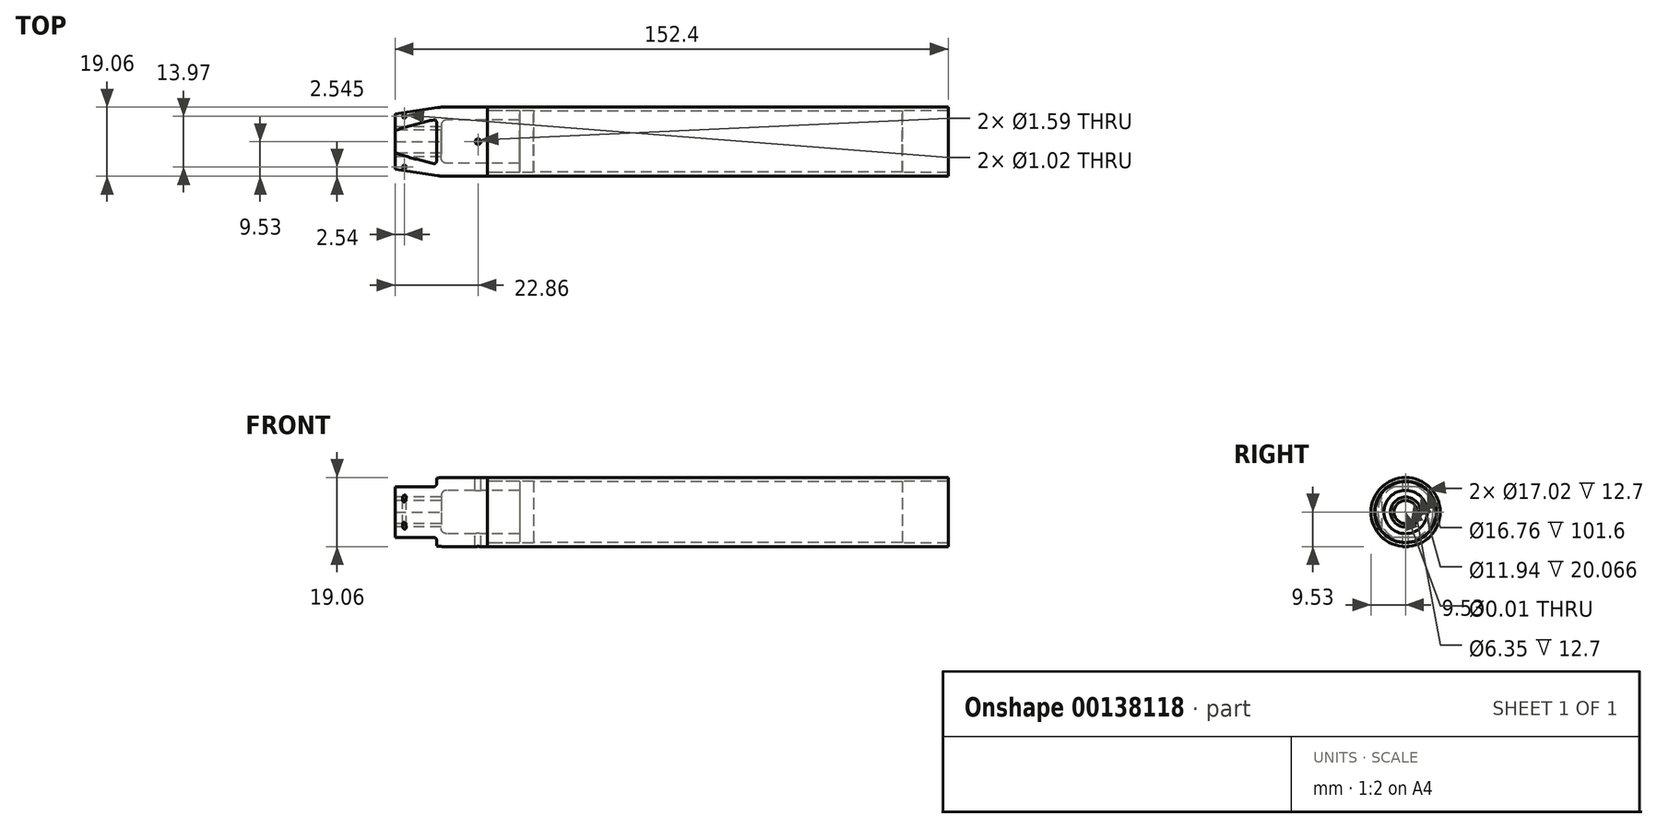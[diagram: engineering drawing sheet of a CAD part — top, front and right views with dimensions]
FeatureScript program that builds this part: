
annotation { "Feature Type Name" : "Feature", "Feature Type Description" : "" }
export const myFeature = defineFeature(function(context is Context, id is Id, definition is map)
    precondition{}
    {
        {
            var Q0;
            Q0=qCreatedBy(makeId("Top.planeOp"),FACE);
            var sketch = newSketch(context, id + "F0", { "sketchPlane" : qUnion([Q0])});
            skLineSegment(sketch, "E0.bottom", {"start": v(0, 9.53) * mm, "end": v(127, 9.53) * mm});
            skLineSegment(sketch, "E0.top", {"start": v(12.7, 8.38) * mm, "end": v(114.3, 8.38) * mm});
            skLineSegment(sketch, "E0.left", {"start": v(0, 9.53) * mm, "end": v(0, 8.5) * mm});
            skLineSegment(sketch, "E0.right", {"start": v(127, 9.53) * mm, "end": v(127, 8.5) * mm});
            skLineSegment(sketch, "E1", {"start": v(0, 8.5) * mm, "end": v(12.7, 8.5) * mm});
            skLineSegment(sketch, "E2", {"start": v(12.7, 8.5) * mm, "end": v(12.7, 8.38) * mm});
            skLineSegment(sketch, "E3", {"start": v(127, 8.5) * mm, "end": v(114.3, 8.5) * mm});
            skLineSegment(sketch, "E4", {"start": v(114.3, 8.5) * mm, "end": v(114.3, 8.38) * mm});
            skSolve(sketch);
        }
        {
            var Q0;
            Q0=qCreatedBy(makeId("Top.planeOp"),FACE);
            var sketch = newSketch(context, id + "F1", { "sketchPlane" : qUnion([Q0])});
            skLineSegment(sketch, "E5", {"start": v(0, 0) * mm, "end": v(25.4, 0) * mm});
            skSolve(sketch);
        }
        {
            var Q0;
            Q0 = qSketchRegion(id + "F0", true);
            var Q1;
            Q1=sQuery(id+"F1.wireOp",EDGE,"E5");
            revolve(context, id + "F2", {"entities" : qUnion([Q0]), "axis" : qUnion([Q1]), "revolveType" : RevolveType.FULL});
        }
        {
            var Q0;
            Q0=qCreatedBy(makeId("Top.planeOp"),FACE);
            var sketch = newSketch(context, id + "F3", { "sketchPlane" : qUnion([Q0])});
            skLineSegment(sketch, "E6", {"start": v(-25.4, 0) * mm, "end": v(-25.4, 7.62) * mm});
            skLineSegment(sketch, "E7", {"start": v(0, 9.53) * mm, "end": v(-12.7, 9.52) * mm});
            skLineSegment(sketch, "E8", {"start": v(-12.7, 9.52) * mm, "end": v(-25.4, 7.62) * mm});
            skLineSegment(sketch, "E9", {"start": v(-25.4, 0) * mm, "end": v(-12.7, 0) * mm});
            skLineSegment(sketch, "E10", {"start": v(-12.7, 0) * mm, "end": v(-12.7, 4.44) * mm});
            skLineSegment(sketch, "E11", {"start": v(-11.18, 5.97) * mm, "end": v(8.9, 5.97) * mm});
            skLineSegment(sketch, "E12", {"start": v(0, 8.5) * mm, "end": v(8.9, 8.5) * mm});
            skLineSegment(sketch, "E13.trimOffspring", {"start": v(0, 8.5) * mm, "end": v(0, 9.53) * mm});
            skPoint(sketch, "E14.0.start.orphan", {"position": v(0, -9.53) * mm});
            skLineSegment(sketch, "E15", {"start": v(8.9, 5.97) * mm, "end": v(8.9, 8.5) * mm});
            skPoint(sketch, "E16.visualSharp", {"position": v(-12.7, 5.97) * mm});
            skArc(sketch, "E16.filletArc", {"start": v(-11.18, 5.97) * mm, "mid": v(-12.25, 5.52) * mm, "end": v(-12.7, 4.44) * mm});
            skSolve(sketch);
        }
        {
            var Q0;
            Q0 = qSketchRegion(id + "F3", true);
            var Q1;
            Q1=sQuery(id+"F1.wireOp",EDGE,"E5");
            revolve(context, id + "F4", {"entities" : qUnion([Q0]), "axis" : qUnion([Q1]), "revolveType" : RevolveType.FULL});
        }
        {
            var Q0;
            Q0=makeQuery(id+"F4.opRevolve","SWEPT_FACE",FACE,{"disambiguationData":[OSD([sQuery(id+"F3.wireOp",EDGE,"E6")])]});
            var sketch = newSketch(context, id + "F5", { "sketchPlane" : qUnion([Q0])});
            skPoint(sketch, "E17", {"position": v(0, 0) * mm});
            skSolve(sketch);
        }
        {
            var Q0;
            Q0=sQuery(id+"F5.wireOp",VERTEX,"E17");
            var Q1;
            Q1=makeQuery(id+"F4.opRevolve","SWEPT_BODY",BODY,{"disambiguationData":[OSD([sQuery(id+"F3.wireOp",EDGE,"E6"),sQuery(id+"F3.wireOp",EDGE,"E7"),sQuery(id+"F3.wireOp",EDGE,"E8"),sQuery(id+"F3.wireOp",EDGE,"E9"),sQuery(id+"F3.wireOp",EDGE,"E10"),sQuery(id+"F3.wireOp",EDGE,"E11"),sQuery(id+"F3.wireOp",EDGE,"E12"),sQuery(id+"F3.wireOp",EDGE,"E13.trimOffspring"),sQuery(id+"F3.wireOp",EDGE,"E15"),sQuery(id+"F3.wireOp",EDGE,"E16.filletArc")])]});
            hole(context, id + "F6", {"style" : HoleStyle.SIMPLE, "endStyle" : HoleEndStyle.THROUGH, "standardTappedOrClearance" : lookupTablePath({ "standard" : "ANSI", "size" : "21/64 (0.33)", "type" : "Drilled" }), "standardBlindInLast" : lookupTablePath({ "standard" : "ANSI", "size" : "21/64", "type" : "Drilled" }), "holeDiameter" : 21 / 1625.6 * mm, "locations" : qUnion([Q0]), "scope" : qUnion([Q1]), "isTappedThrough" : true});
        }
        {
            var Q0;
            Q0=qCreatedBy(makeId("Top.planeOp"),FACE);
            var sketch = newSketch(context, id + "F7", { "sketchPlane" : qUnion([Q0])});
            skCircle(sketch, "E18", {"center": v(-2.54, 0) * mm, "radius": 0.8 * mm});
            skSolve(sketch);
        }
        {
            var Q0;
            Q0 = qSketchRegion(id + "F7", true);
            extrude(context, id + "F8", {"entities" : qUnion([Q0]), "operationType" : NewBodyOperationType.REMOVE, "endBound" : BoundingType.THROUGH_ALL, "oppositeDirection" : true, "depth" : 25.4 * mm, "hasSecondDirection" : true, "secondDirectionBound" : BoundingType.THROUGH_ALL, "secondDirectionOppositeDirection" : false, "secondDirectionDepth" : 25.4 * mm});
        }
        {
            var Q0;
            Q0=makeQuery(id+"F4.opRevolve","SWEPT_EDGE",EDGE,{"disambiguationData":[OSD([sQuery(id+"F3.wireOp",EDGE,"E7"),sQuery(id+"F3.wireOp",EDGE,"E8")])]});
            fillet(context, id + "F9", {"entities" : qUnion([Q0]), "radius" : 12.7 * mm, "tangentPropagation" : true, "allowEdgeOverflow" : false});
        }
        {
            var Q0;
            Q0=makeQuery(id+"F4.opRevolve","SWEPT_FACE",FACE,{"disambiguationData":[OSD([sQuery(id+"F3.wireOp",EDGE,"E6")])]});
            var sketch = newSketch(context, id + "F10", { "sketchPlane" : qUnion([Q0])});
            skCircle(sketch, "E19", {"center": v(0, 0) * mm, "radius": 4.14 * mm});
            skCircle(sketch, "E20", {"center": v(0, 0) * mm, "radius": 3.18 * mm});
            skSolve(sketch);
        }
        {
            var Q0;
            Q0 = qSketchRegion(id + "F10", true);
            extrude(context, id + "F11", {"entities" : qUnion([Q0]), "oppositeDirection" : true, "depth" : 12.7 * mm});
        }
        {
            var Q0;
            Q0=makeQuery(id+"F4.opRevolve","SWEPT_FACE",FACE,{"disambiguationData":[OSD([sQuery(id+"F3.wireOp",EDGE,"E6")])]});
            var sketch = newSketch(context, id + "F12", { "sketchPlane" : qUnion([Q0])});
            skLineSegment(sketch, "E21", {"start": v(-6.48, 6.99) * mm, "end": v(6.48, 6.99) * mm});
            skLineSegment(sketch, "E22", {"start": v(-6.48, -6.99) * mm, "end": v(6.48, -6.99) * mm});
            skArc(sketch, "E23.0", {"start": v(6.48, 6.99) * mm, "mid": v(0, 9.52) * mm, "end": v(-6.48, 6.99) * mm});
            skArc(sketch, "E24.trimOffspring", {"start": v(-6.48, -6.99) * mm, "mid": v(0, -9.52) * mm, "end": v(6.48, -6.99) * mm});
            skSolve(sketch);
        }
        {
            var Q0;
            Q0 = qSketchRegion(id + "F12", true);
            extrude(context, id + "F13", {"entities" : qUnion([Q0]), "operationType" : NewBodyOperationType.REMOVE, "oppositeDirection" : true, "depth" : 11.43 * mm});
        }
        {
            var Q0;
            Q0=makeQuery(id+"F13.boolean.opBoolean","COPY",EDGE,{"derivedFrom":makeQuery(id+"F13.opExtrude","CAP_EDGE",EDGE,{"disambiguationData":[OSD([sQuery(id+"F12.wireOp",EDGE,"E21")])],"isStart":false})});
            var Q1;
            Q1=makeQuery(id+"F13.boolean.opBoolean","COPY",EDGE,{"derivedFrom":makeQuery(id+"F13.opExtrude","CAP_EDGE",EDGE,{"disambiguationData":[OSD([sQuery(id+"F12.wireOp",EDGE,"E22")])],"isStart":false})});
            fillet(context, id + "F14", {"entities" : qUnion([Q0, Q1]), "radius" : 0.76 * mm, "tangentPropagation" : true, "allowEdgeOverflow" : false});
        }
        {
            var Q0;
            Q0=makeQuery(id+"F13.boolean.opBoolean","COPY",FACE,{"derivedFrom":makeQuery(id+"F13.opExtrude","SWEPT_FACE",FACE,{"disambiguationData":[OSD([sQuery(id+"F12.wireOp",EDGE,"E21")])]})});
            var sketch = newSketch(context, id + "F15", { "sketchPlane" : qUnion([Q0])});
            skCircle(sketch, "E25", {"center": v(-22.86, 6.99) * mm, "radius": 0.5 * mm});
            skCircle(sketch, "E26", {"center": v(-22.86, -6.99) * mm, "radius": 0.5 * mm});
            skSolve(sketch);
        }
        {
            var Q0;
            Q0 = qSketchRegion(id + "F15", true);
            extrude(context, id + "F16", {"entities" : qUnion([Q0]), "operationType" : NewBodyOperationType.REMOVE, "endBound" : BoundingType.THROUGH_ALL, "oppositeDirection" : true, "depth" : 25.4 * mm});
        }
    });
